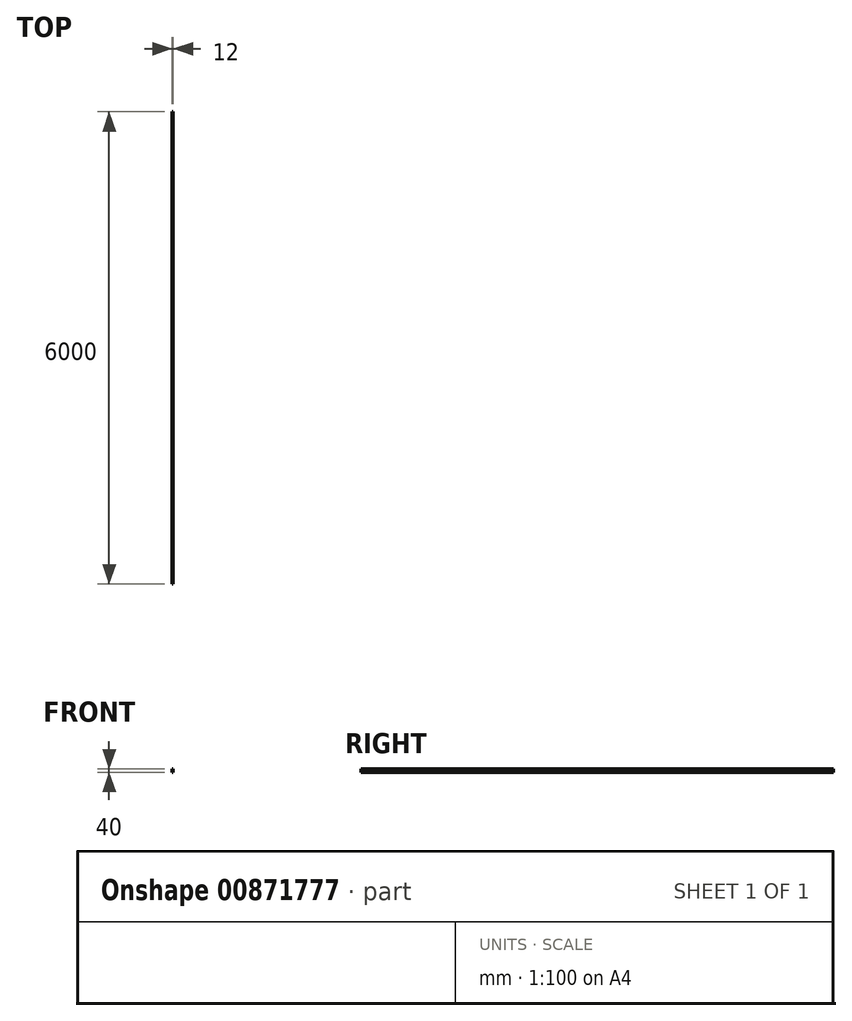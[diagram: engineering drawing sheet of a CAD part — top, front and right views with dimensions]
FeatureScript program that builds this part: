
annotation { "Feature Type Name" : "Feature", "Feature Type Description" : "" }
export const myFeature = defineFeature(function(context is Context, id is Id, definition is map)
    precondition{}
    {
        {
            var Q0;
            Q0=qCreatedBy(makeId("Front.planeOp"),FACE);
            var sketch = newSketch(context, id + "F0", { "sketchPlane" : qUnion([Q0])});
            skLineSegment(sketch, "E0.bottom", {"start": v(0, 0) * mm, "end": v(12, 0) * mm});
            skLineSegment(sketch, "E0.top", {"start": v(0, 40) * mm, "end": v(12, 40) * mm});
            skLineSegment(sketch, "E0.left", {"start": v(0, 0) * mm, "end": v(0, 40) * mm});
            skLineSegment(sketch, "E0.right", {"start": v(12, 0) * mm, "end": v(12, 40) * mm});
            skSolve(sketch);
        }
        {
            var Q0;
            Q0 = qSketchRegion(id + "F0", true);
            extrude(context, id + "F1", {"entities" : qUnion([Q0]), "depth" : 6000 * mm, "offsetDistance" : 25 * mm});
        }
    });
